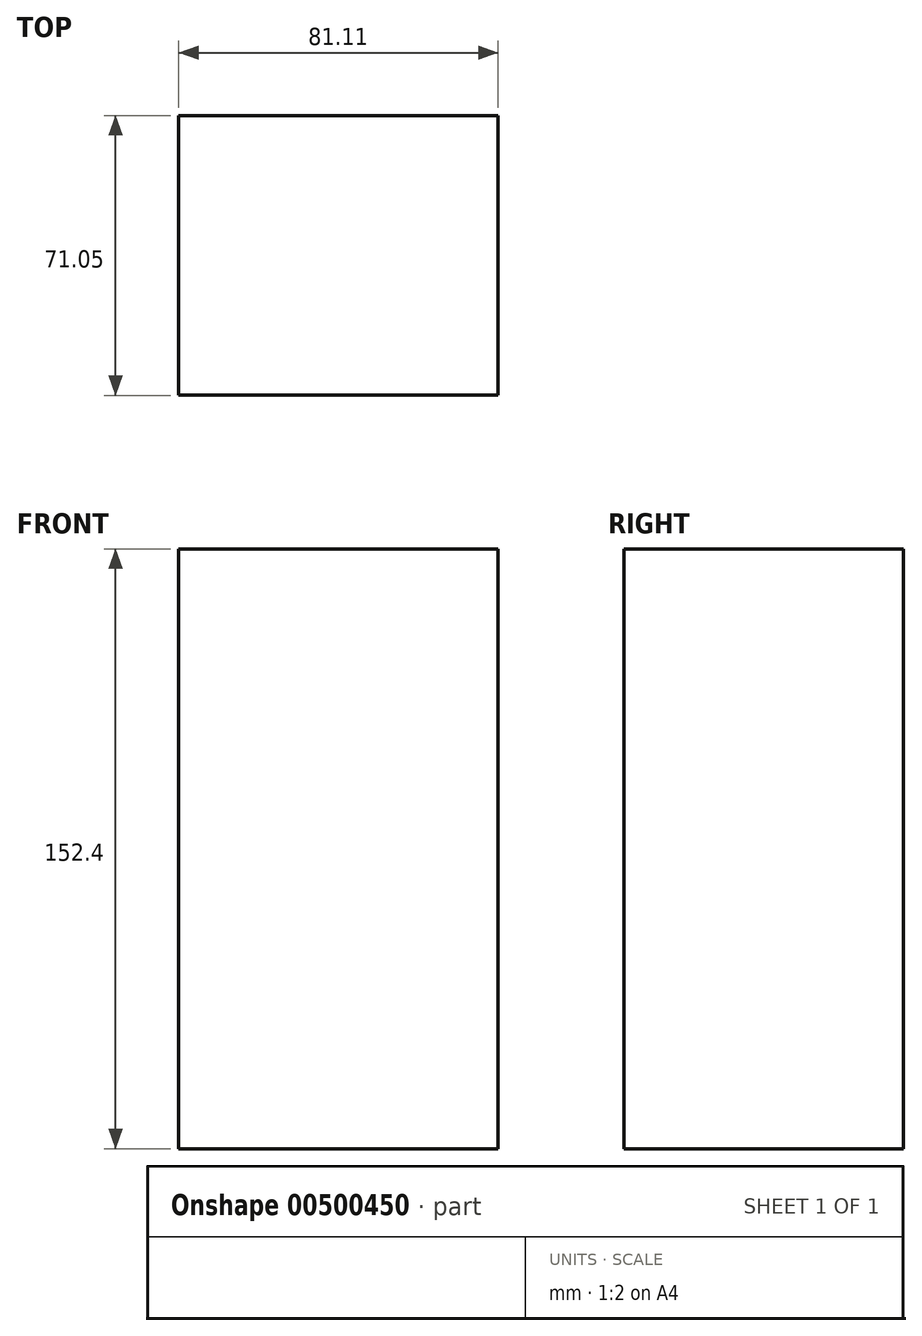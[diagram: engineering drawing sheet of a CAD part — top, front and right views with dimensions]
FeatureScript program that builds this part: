
annotation { "Feature Type Name" : "Feature", "Feature Type Description" : "" }
export const myFeature = defineFeature(function(context is Context, id is Id, definition is map)
    precondition{}
    {
        {
            var Q0;
            Q0=qCreatedBy(makeId("Top.planeOp"),FACE);
            var sketch = newSketch(context, id + "F0", { "sketchPlane" : qUnion([Q0])});
            skLineSegment(sketch, "E0.bottom", {"start": v(-44.64, 37.25) * mm, "end": v(36.47, 37.25) * mm});
            skLineSegment(sketch, "E0.top", {"start": v(-44.64, -33.8) * mm, "end": v(36.47, -33.8) * mm});
            skLineSegment(sketch, "E0.left", {"start": v(-44.64, 37.25) * mm, "end": v(-44.64, -33.8) * mm});
            skLineSegment(sketch, "E0.right", {"start": v(36.47, 37.25) * mm, "end": v(36.47, -33.8) * mm});
            skSolve(sketch);
        }
        {
            var Q0;
            Q0=makeQuery(id+"F0.imprint","IMPRINT",FACE,{"disambiguationData":[TD([[makeQuery(id+"F0.imprint","IMPRINT",EDGE,{"derivedFrom":sQuery(id+"F0.wireOp",EDGE,"E0.bottom")}),-1.0]])]});
            extrude(context, id + "F1", {"entities" : qUnion([Q0]), "depth" : 152.4 * mm});
        }
    });
